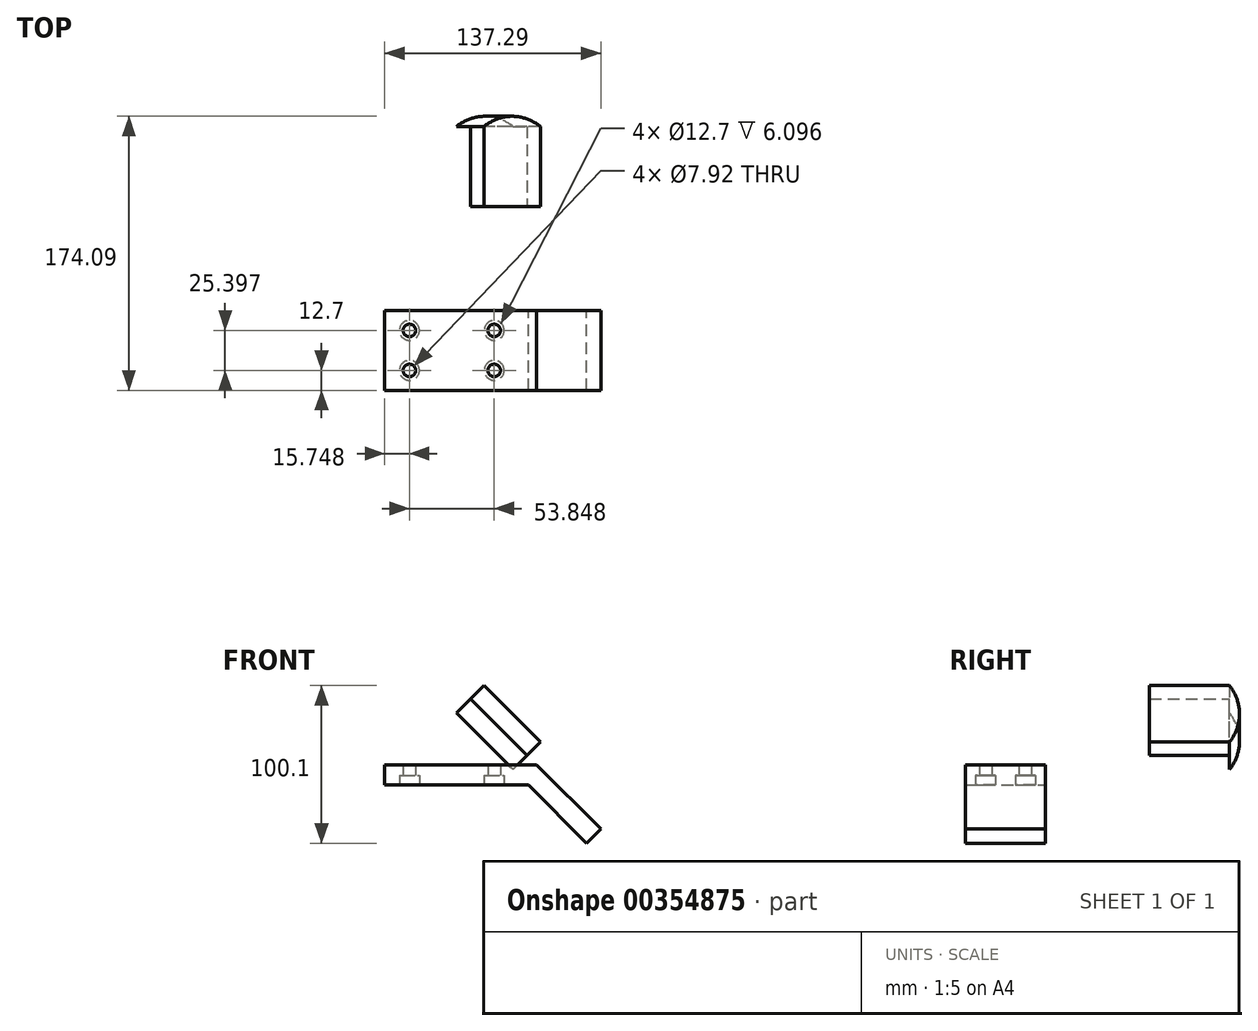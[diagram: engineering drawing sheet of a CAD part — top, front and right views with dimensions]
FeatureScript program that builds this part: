
annotation { "Feature Type Name" : "Feature", "Feature Type Description" : "" }
export const myFeature = defineFeature(function(context is Context, id is Id, definition is map)
    precondition{}
    {
        {
            var Q0;
            Q0=qCreatedBy(makeId("Front.planeOp"),FACE);
            var sketch = newSketch(context, id + "F0", { "sketchPlane" : qUnion([Q0])});
            skLineSegment(sketch, "E0", {"start": v(0, 0) * mm, "end": v(0, 12.7) * mm});
            skLineSegment(sketch, "E1", {"start": v(0, 12.7) * mm, "end": v(96.52, 12.7) * mm});
            skLineSegment(sketch, "E2", {"start": v(96.52, 12.7) * mm, "end": v(96.52, 0) * mm});
            skLineSegment(sketch, "E3", {"start": v(96.52, 0) * mm, "end": v(0, 0) * mm});
            skLineSegment(sketch, "E4", {"start": v(96.52, 12.7) * mm, "end": v(87.54, 3.72) * mm});
            skLineSegment(sketch, "E5", {"start": v(87.54, 3.72) * mm, "end": v(128.31, -37.05) * mm});
            skLineSegment(sketch, "E6", {"start": v(128.31, -37.05) * mm, "end": v(137.3, -28.07) * mm});
            skLineSegment(sketch, "E7", {"start": v(137.3, -28.07) * mm, "end": v(96.52, 12.7) * mm});
            skSolve(sketch);
        }
        {
            var Q0;
            Q0 = qSketchRegion(id + "F0", true);
            extrude(context, id + "F1", {"entities" : qUnion([Q0]), "depth" : 50.8 * mm});
        }
        {
            var Q0;
            Q0=makeQuery(id+"F1.opExtrude","SWEPT_FACE",FACE,{"disambiguationData":[OSD([sQuery(id+"F0.wireOp",EDGE,"E7")])]});
            var sketch = newSketch(context, id + "F2", { "sketchPlane" : qUnion([Q0])});
            skLineSegment(sketch, "E8", {"start": v(116.93, -50.8) * mm, "end": v(116.93, 0) * mm});
            skArc(sketch, "E9", {"start": v(116.93, -50.8) * mm, "mid": v(123.3, -25.4) * mm, "end": v(116.93, 0) * mm});
            skSolve(sketch);
        }
        {
            var Q0;
            Q0 = qSketchRegion(id + "F2", true);
            extrude(context, id + "F3", {"entities" : qUnion([Q0]), "operationType" : NewBodyOperationType.ADD, "oppositeDirection" : true, "depth" : 12.7 * mm});
        }
        {
            var Q0;
            Q0=makeQuery(id+"F3.boolean.opBoolean","MERGE",FACE,{"derivedFrom":[makeQuery(id+"F1.opExtrude","SWEPT_FACE",FACE,{"disambiguationData":[OSD([sQuery(id+"F0.wireOp",EDGE,"E7")])]}),makeQuery(id+"F3.opExtrude","CAP_FACE",FACE,{"disambiguationData":[OSD([sQuery(id+"F2.wireOp",EDGE,"E9"),sQuery(id+"F2.wireOp",EDGE,"E8")])],"isStart":true})]});
            var sketch = newSketch(context, id + "F4", { "sketchPlane" : qUnion([Q0])});
            skArc(sketch, "E10", {"start": v(116.93, -50.8) * mm, "mid": v(123.3, -25.4) * mm, "end": v(116.93, 0) * mm});
            skLineSegment(sketch, "E11", {"start": v(116.93, -50.8) * mm, "end": v(66.13, -50.8) * mm});
            skLineSegment(sketch, "E12", {"start": v(66.13, -50.8) * mm, "end": v(66.13, 0) * mm});
            skLineSegment(sketch, "E13", {"start": v(66.13, 0) * mm, "end": v(116.93, 0) * mm});
            skSolve(sketch);
        }
        {
            var Q0;
            Q0 = qSketchRegion(id + "F4", true);
            extrude(context, id + "F5", {"entities" : qUnion([Q0]), "operationType" : NewBodyOperationType.ADD, "depth" : 11.94 * mm});
        }
        {
            var Q0;
            Q0=makeQuery(id+"F5.opExtrude","SWEPT_FACE",FACE,{"disambiguationData":[OSD([sQuery(id+"F4.wireOp",EDGE,"E12")])]});
            var sketch = newSketch(context, id + "F6", { "sketchPlane" : qUnion([Q0])});
            skLineSegment(sketch, "E14", {"start": v(25.4, 89.17) * mm, "end": v(35.05, 89.17) * mm});
            skLineSegment(sketch, "E15", {"start": v(25.4, 89.17) * mm, "end": v(15.75, 89.17) * mm});
            skLineSegment(sketch, "E16", {"start": v(15.75, 89.17) * mm, "end": v(15.75, 83.07) * mm});
            skLineSegment(sketch, "E17", {"start": v(15.75, 83.07) * mm, "end": v(9.65, 83.07) * mm});
            skLineSegment(sketch, "E18", {"start": v(9.65, 83.07) * mm, "end": v(9.65, 76.47) * mm});
            skLineSegment(sketch, "E19", {"start": v(9.65, 76.47) * mm, "end": v(41.15, 76.47) * mm});
            skLineSegment(sketch, "E20", {"start": v(41.15, 76.47) * mm, "end": v(41.15, 83.07) * mm});
            skLineSegment(sketch, "E21", {"start": v(41.15, 83.07) * mm, "end": v(35.05, 83.07) * mm});
            skLineSegment(sketch, "E22", {"start": v(35.05, 83.07) * mm, "end": v(35.05, 89.17) * mm});
            skSolve(sketch);
        }
        {
            var Q0;
            Q0 = qSketchRegion(id + "F6", true);
            extrude(context, id + "F7", {"entities" : qUnion([Q0]), "operationType" : NewBodyOperationType.REMOVE, "oppositeDirection" : true, "depth" : 76.2 * mm});
        }
        {
            var Q0;
            Q0=makeQuery(id+"F1.opExtrude","SWEPT_FACE",FACE,{"disambiguationData":[OSD([sQuery(id+"F0.wireOp",EDGE,"E3")])]});
            var sketch = newSketch(context, id + "F8", { "sketchPlane" : qUnion([Q0])});
            skLineSegment(sketch, "E23.bottom", {"start": v(0, 50.8) * mm, "end": v(91.26, 50.8) * mm, "construction": true});
            skLineSegment(sketch, "E23.top", {"start": v(0, 0) * mm, "end": v(91.26, 0) * mm, "construction": true});
            skLineSegment(sketch, "E23.left", {"start": v(0, 50.8) * mm, "end": v(0, 0) * mm, "construction": true});
            skLineSegment(sketch, "E23.right", {"start": v(91.26, 50.8) * mm, "end": v(91.26, 0) * mm, "construction": true});
            skLineSegment(sketch, "E24", {"start": v(0, 50.8) * mm, "end": v(0, 38.1) * mm, "construction": true});
            skLineSegment(sketch, "E25", {"start": v(0, 38.1) * mm, "end": v(15.75, 38.1) * mm, "construction": true});
            skCircle(sketch, "E26", {"center": v(15.75, 38.1) * mm, "radius": 6.35 * mm});
            skLineSegment(sketch, "E27", {"start": v(15.75, 38.1) * mm, "end": v(15.75, 12.7) * mm, "construction": true});
            skCircle(sketch, "E28", {"center": v(15.75, 12.7) * mm, "radius": 6.35 * mm});
            skLineSegment(sketch, "E29", {"start": v(15.75, 12.7) * mm, "end": v(0, 12.7) * mm, "construction": true});
            skLineSegment(sketch, "E30", {"start": v(0, 12.7) * mm, "end": v(0, 0) * mm, "construction": true});
            skLineSegment(sketch, "E31", {"start": v(0, 38.1) * mm, "end": v(0, 12.7) * mm, "construction": true});
            skLineSegment(sketch, "E32", {"start": v(15.75, 38.1) * mm, "end": v(69.6, 38.1) * mm, "construction": true});
            skLineSegment(sketch, "E33", {"start": v(69.6, 38.1) * mm, "end": v(69.6, 12.7) * mm, "construction": true});
            skLineSegment(sketch, "E34", {"start": v(69.6, 12.7) * mm, "end": v(15.75, 12.7) * mm, "construction": true});
            skCircle(sketch, "E35", {"center": v(69.6, 38.1) * mm, "radius": 6.35 * mm});
            skCircle(sketch, "E36", {"center": v(69.6, 12.7) * mm, "radius": 6.35 * mm});
            skSolve(sketch);
        }
        {
            var Q0;
            Q0 = qSketchRegion(id + "F8", true);
            extrude(context, id + "F9", {"entities" : qUnion([Q0]), "operationType" : NewBodyOperationType.REMOVE, "oppositeDirection" : true, "depth" : 6.1 * mm});
        }
        {
            var Q0;
            Q0=makeQuery(id+"F1.opExtrude","SWEPT_FACE",FACE,{"disambiguationData":[OSD([sQuery(id+"F0.wireOp",EDGE,"E3")])]});
            var sketch = newSketch(context, id + "F10", { "sketchPlane" : qUnion([Q0])});
            skPoint(sketch, "E37", {"position": v(15.75, 38.1) * mm});
            skPoint(sketch, "E38", {"position": v(69.6, 38.1) * mm});
            skPoint(sketch, "E39", {"position": v(69.6, 12.7) * mm});
            skPoint(sketch, "E40", {"position": v(15.75, 12.7) * mm});
            skSolve(sketch);
        }
        {
            var Q0;
            Q0=sQuery(id+"F10.wireOp",VERTEX,"E37");
            var Q1;
            Q1=sQuery(id+"F10.wireOp",VERTEX,"E38");
            var Q2;
            Q2=sQuery(id+"F10.wireOp",VERTEX,"E39");
            var Q3;
            Q3=sQuery(id+"F10.wireOp",VERTEX,"E40");
            var Q4;
            Q4=makeQuery(id+"F1.opExtrude","SWEPT_BODY",BODY,{"disambiguationData":[OSD([sQuery(id+"F0.wireOp",EDGE,"E0"),sQuery(id+"F0.wireOp",EDGE,"E1"),sQuery(id+"F0.wireOp",EDGE,"E3"),sQuery(id+"F0.wireOp",EDGE,"E5"),sQuery(id+"F0.wireOp",EDGE,"E6"),sQuery(id+"F0.wireOp",EDGE,"E7")])]});
            hole(context, id + "F11", {"style" : HoleStyle.C_BORE, "endStyle" : HoleEndStyle.THROUGH, "holeDiameter" : 7.92 * mm, "cBoreDiameter" : 12.7 * mm, "cBoreDepth" : 6.1 * mm, "isTappedThrough" : true, "tappedDepth" : 12.7 * mm, "tapClearance" : 3, "locations" : qUnion([Q0, Q1, Q2, Q3]), "scope" : qUnion([Q4])});
        }
    });
